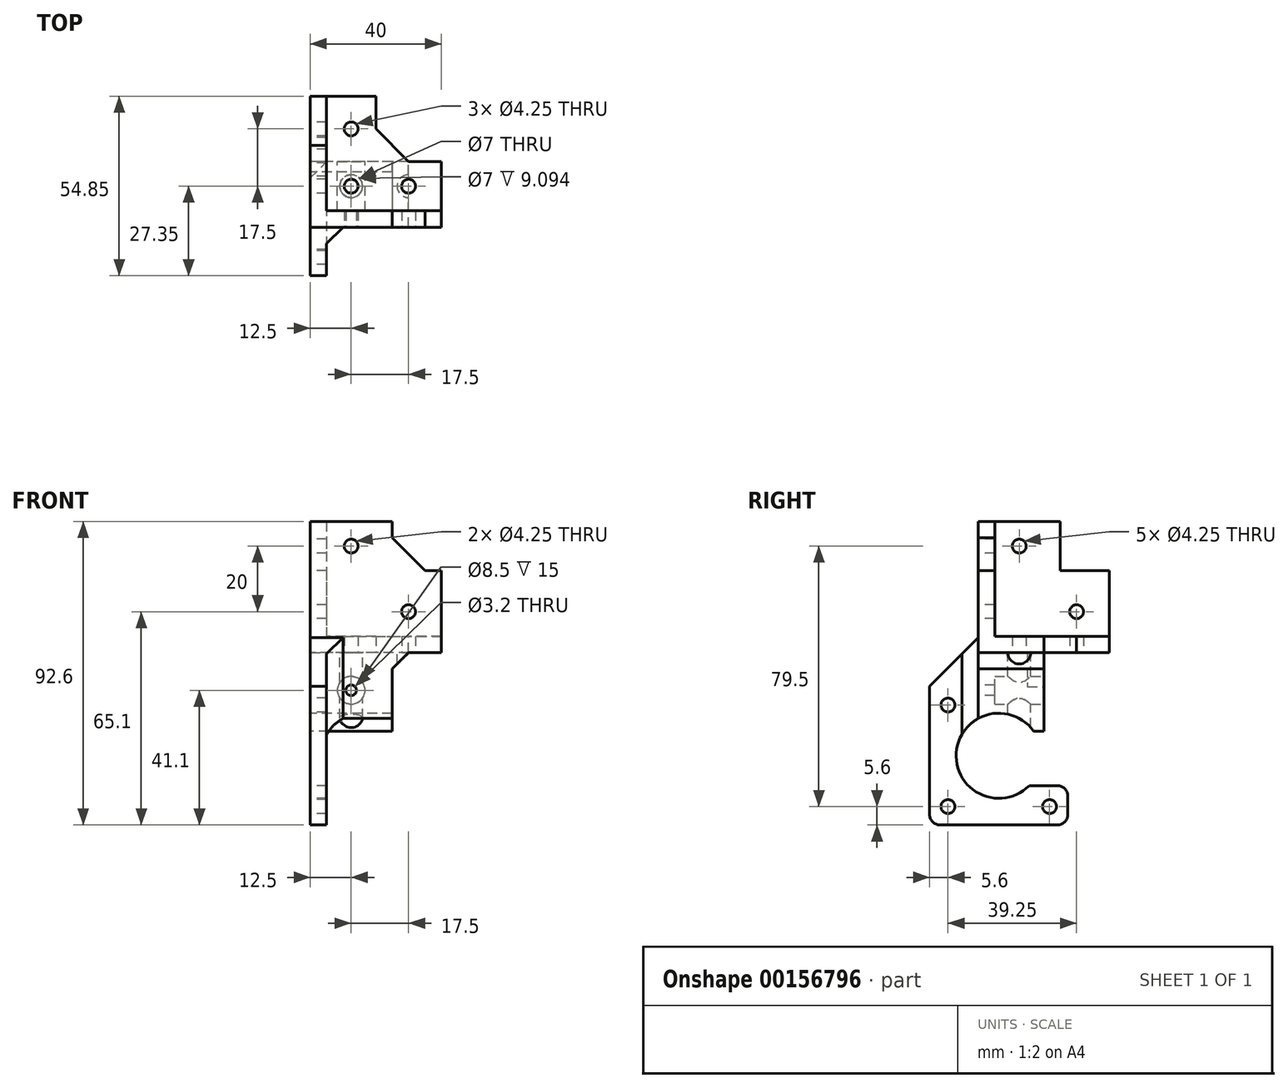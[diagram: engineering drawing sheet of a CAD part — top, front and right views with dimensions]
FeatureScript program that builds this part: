
annotation { "Feature Type Name" : "Feature", "Feature Type Description" : "" }
export const myFeature = defineFeature(function(context is Context, id is Id, definition is map)
    precondition{}
    {
        {
            var Q0;
            Q0=qCreatedBy(makeId("Top.planeOp"),FACE);
            var sketch = newSketch(context, id + "F0", { "sketchPlane" : qUnion([Q0])});
            skLineSegment(sketch, "E0", {"start": v(0, 40) * mm, "end": v(-20, 40) * mm});
            skLineSegment(sketch, "E1", {"start": v(-20, 40) * mm, "end": v(-20, 0) * mm});
            skLineSegment(sketch, "E2", {"start": v(-20, 0) * mm, "end": v(20, 0) * mm});
            skLineSegment(sketch, "E3", {"start": v(20, 0) * mm, "end": v(20, 20) * mm});
            skLineSegment(sketch, "E4", {"start": v(20, 20) * mm, "end": v(0, 20) * mm});
            skLineSegment(sketch, "E5", {"start": v(0, 20) * mm, "end": v(0, 40) * mm});
            skCircle(sketch, "E6", {"center": v(-7.5, 30) * mm, "radius": 2.12 * mm});
            skCircle(sketch, "E7", {"center": v(10, 12.5) * mm, "radius": 2.12 * mm});
            skCircle(sketch, "E8", {"center": v(-7.5, 12.5) * mm, "radius": 2.12 * mm});
            skSolve(sketch);
        }
        {
            var Q0;
            Q0=qSketchRegion(id+"F0",true);
            extrude(context, id + "F1", {"entities" : qUnion([Q0]), "depth" : 5 * mm});
        }
        {
            var Q0;
            Q0=makeQuery(id+"F1.opExtrude","CAP_FACE",FACE,{"disambiguationData":[OSD([sQuery(id+"F0.wireOp",EDGE,"E0"),sQuery(id+"F0.wireOp",EDGE,"E1"),sQuery(id+"F0.wireOp",EDGE,"E2"),sQuery(id+"F0.wireOp",EDGE,"E3"),sQuery(id+"F0.wireOp",EDGE,"E4"),sQuery(id+"F0.wireOp",EDGE,"E5"),sQuery(id+"F0.wireOp",EDGE,"E6"),sQuery(id+"F0.wireOp",EDGE,"E7")])],"isStart":false});
            var sketch = newSketch(context, id + "F2", { "sketchPlane" : qUnion([Q0])});
            skLineSegment(sketch, "E9", {"start": v(-20, 40) * mm, "end": v(-15, 40) * mm});
            skLineSegment(sketch, "E10", {"start": v(-15, 40) * mm, "end": v(-15, 5) * mm});
            skLineSegment(sketch, "E11", {"start": v(-15, 5) * mm, "end": v(20, 5) * mm});
            skLineSegment(sketch, "E12", {"start": v(20, 5) * mm, "end": v(20, 0) * mm});
            skLineSegment(sketch, "E13", {"start": v(20, 0) * mm, "end": v(-20, 0) * mm});
            skLineSegment(sketch, "E14", {"start": v(-20, 0) * mm, "end": v(-20, 40) * mm});
            skSolve(sketch);
        }
        {
            var Q0;
            Q0=qSketchRegion(id+"F2",true);
            extrude(context, id + "F3", {"entities" : qUnion([Q0]), "operationType" : NewBodyOperationType.ADD, "depth" : 20 * mm});
        }
        {
            var Q0;
            Q0=makeQuery(id+"F3.opExtrude","CAP_FACE",FACE,{"disambiguationData":[OSD([sQuery(id+"F2.wireOp",EDGE,"E9"),sQuery(id+"F2.wireOp",EDGE,"E10"),sQuery(id+"F2.wireOp",EDGE,"E11"),sQuery(id+"F2.wireOp",EDGE,"E12"),sQuery(id+"F2.wireOp",EDGE,"E13"),sQuery(id+"F2.wireOp",EDGE,"E14")])],"isStart":false});
            var sketch = newSketch(context, id + "F4", { "sketchPlane" : qUnion([Q0])});
            skLineSegment(sketch, "E15", {"start": v(-15, 25) * mm, "end": v(-20, 25) * mm});
            skLineSegment(sketch, "E16", {"start": v(-20, 25) * mm, "end": v(-20, 0) * mm});
            skLineSegment(sketch, "E17", {"start": v(-20, 0) * mm, "end": v(5, 0) * mm});
            skLineSegment(sketch, "E18", {"start": v(5, 0) * mm, "end": v(5, 5) * mm});
            skLineSegment(sketch, "E19", {"start": v(5, 5) * mm, "end": v(-15, 5) * mm});
            skLineSegment(sketch, "E20", {"start": v(-15, 5) * mm, "end": v(-15, 25) * mm});
            skSolve(sketch);
        }
        {
            var Q0;
            Q0=qSketchRegion(id+"F4",true);
            extrude(context, id + "F5", {"entities" : qUnion([Q0]), "operationType" : NewBodyOperationType.ADD, "depth" : 15 * mm});
        }
        {
            var Q0;
            Q0=makeQuery(id+"F1.opExtrude","SWEPT_EDGE",EDGE,{"disambiguationData":[OSD([sQuery(id+"F0.wireOp",EDGE,"E4"),sQuery(id+"F0.wireOp",EDGE,"E5")])]});
            var Q1;
            Q1=makeQuery(id+"F5.opExtrude","CAP_EDGE",EDGE,{"disambiguationData":[OSD([sQuery(id+"F4.wireOp",EDGE,"E15")])],"isStart":true});
            var Q2;
            Q2=makeQuery(id+"F5.opExtrude","CAP_EDGE",EDGE,{"disambiguationData":[OSD([sQuery(id+"F4.wireOp",EDGE,"E18")])],"isStart":true});
            chamfer(context, id + "F6", {"entities" : qUnion([Q0, Q1, Q2]), "width" : 10 * mm, "tangentPropagation" : true});
        }
        {
            var Q0;
            Q0=makeQuery(id+"F5.boolean.opBoolean","MERGE",FACE,{"derivedFrom":[makeQuery(id+"F3.boolean.opBoolean","MERGE",FACE,{"derivedFrom":[makeQuery(id+"F1.opExtrude","SWEPT_FACE",FACE,{"disambiguationData":[OSD([sQuery(id+"F0.wireOp",EDGE,"E2")])]}),makeQuery(id+"F3.opExtrude","SWEPT_FACE",FACE,{"disambiguationData":[OSD([sQuery(id+"F2.wireOp",EDGE,"E13")])]})]}),makeQuery(id+"F5.opExtrude","SWEPT_FACE",FACE,{"disambiguationData":[OSD([sQuery(id+"F4.wireOp",EDGE,"E17")])]})]});
            var sketch = newSketch(context, id + "F7", { "sketchPlane" : qUnion([Q0])});
            skCircle(sketch, "E21", {"center": v(-7.5, 32.5) * mm, "radius": 2.12 * mm});
            skCircle(sketch, "E22", {"center": v(10, 12.5) * mm, "radius": 2.12 * mm});
            skSolve(sketch);
        }
        {
            var Q0;
            Q0=qSketchRegion(id+"F7",true);
            extrude(context, id + "F8", {"entities" : qUnion([Q0]), "operationType" : NewBodyOperationType.REMOVE, "oppositeDirection" : true, "depth" : 5 * mm});
        }
        {
            var Q0;
            Q0=makeQuery(id+"F5.boolean.opBoolean","MERGE",FACE,{"derivedFrom":[makeQuery(id+"F3.boolean.opBoolean","MERGE",FACE,{"derivedFrom":[makeQuery(id+"F1.opExtrude","SWEPT_FACE",FACE,{"disambiguationData":[OSD([sQuery(id+"F0.wireOp",EDGE,"E1")])]}),makeQuery(id+"F3.opExtrude","SWEPT_FACE",FACE,{"disambiguationData":[OSD([sQuery(id+"F2.wireOp",EDGE,"E14")])]})]}),makeQuery(id+"F5.opExtrude","SWEPT_FACE",FACE,{"disambiguationData":[OSD([sQuery(id+"F4.wireOp",EDGE,"E16")])]})]});
            var sketch = newSketch(context, id + "F9", { "sketchPlane" : qUnion([Q0])});
            skCircle(sketch, "E23", {"center": v(-12.5, 32.5) * mm, "radius": 2.12 * mm});
            skCircle(sketch, "E24", {"center": v(-30, 12.5) * mm, "radius": 2.12 * mm});
            skSolve(sketch);
        }
        {
            var Q0;
            Q0=qSketchRegion(id+"F9",true);
            extrude(context, id + "F10", {"entities" : qUnion([Q0]), "operationType" : NewBodyOperationType.REMOVE, "oppositeDirection" : true, "depth" : 5 * mm});
        }
        {
            var Q0;
            Q0=makeQuery(id+"F1.opExtrude","CAP_FACE",FACE,{"disambiguationData":[OSD([sQuery(id+"F0.wireOp",EDGE,"E0"),sQuery(id+"F0.wireOp",EDGE,"E1"),sQuery(id+"F0.wireOp",EDGE,"E2"),sQuery(id+"F0.wireOp",EDGE,"E3"),sQuery(id+"F0.wireOp",EDGE,"E4"),sQuery(id+"F0.wireOp",EDGE,"E5"),sQuery(id+"F0.wireOp",EDGE,"E6"),sQuery(id+"F0.wireOp",EDGE,"E7"),sQuery(id+"F0.wireOp",EDGE,"E8")])],"isStart":true});
            var sketch = newSketch(context, id + "F11", { "sketchPlane" : qUnion([Q0])});
            skLineSegment(sketch, "E25.bottom", {"start": v(20, -20) * mm, "end": v(-20, -20) * mm});
            skLineSegment(sketch, "E25.top", {"start": v(20, 0) * mm, "end": v(-20, 0) * mm});
            skLineSegment(sketch, "E25.left", {"start": v(20, -20) * mm, "end": v(20, 0) * mm});
            skLineSegment(sketch, "E25.right", {"start": v(-20, -20) * mm, "end": v(-20, 0) * mm});
            skPoint(sketch, "E25.middle", {"position": v(0, -10) * mm});
            skPoint(sketch, "E26.visualSharp", {"position": v(-20, 0) * mm});
            skLineSegment(sketch, "E26.filletArc", {"start": v(-20, 0) * mm, "end": v(-20, 0) * mm});
            skCircle(sketch, "E27", {"center": v(10, -12.5) * mm, "radius": 2.12 * mm});
            skCircle(sketch, "E28", {"center": v(-7.5, -12.5) * mm, "radius": 2.12 * mm});
            skSolve(sketch);
        }
        {
            var Q0;
            Q0=qSketchRegion(id+"F11",true);
            extrude(context, id + "F12", {"entities" : qUnion([Q0]), "operationType" : NewBodyOperationType.ADD, "depth" : 24 * mm});
        }
        {
            var Q0;
            Q0=makeQuery(id+"F12.boolean.opBoolean","MERGE",FACE,{"derivedFrom":[makeQuery(id+"F1.opExtrude","SWEPT_FACE",FACE,{"disambiguationData":[OSD([sQuery(id+"F0.wireOp",EDGE,"E4")])]}),makeQuery(id+"F12.opExtrude","SWEPT_FACE",FACE,{"disambiguationData":[OSD([sQuery(id+"F11.wireOp",EDGE,"E25.bottom")])]})]});
            var sketch = newSketch(context, id + "F13", { "sketchPlane" : qUnion([Q0])});
            skLineSegment(sketch, "E29", {"start": v(20, -11.5) * mm, "end": v(20, -24) * mm});
            skLineSegment(sketch, "E30", {"start": v(20, -24) * mm, "end": v(7.5, -24) * mm});
            skPoint(sketch, "E31.orphan", {"position": v(7.5, -24) * mm});
            skCircle(sketch, "E32", {"center": v(7.5, -11.5) * mm, "radius": 4.25 * mm});
            skLineSegment(sketch, "E33", {"start": v(-5, -11.5) * mm, "end": v(-5, 0) * mm});
            skLineSegment(sketch, "E34", {"start": v(-5, 0) * mm, "end": v(-20, 0) * mm});
            skLineSegment(sketch, "E35", {"start": v(-20, 0) * mm, "end": v(-20, -24) * mm});
            skLineSegment(sketch, "E36", {"start": v(-20, -24) * mm, "end": v(7.5, -24) * mm});
            skLineSegment(sketch, "E37", {"start": v(-5, -11.5) * mm, "end": v(-5, -24) * mm});
            skSolve(sketch);
        }
        {
            var Q0;
            Q0=qSketchRegion(id+"F13",true);
            extrude(context, id + "F14", {"entities" : qUnion([Q0]), "operationType" : NewBodyOperationType.REMOVE, "oppositeDirection" : true, "depth" : 25 * mm});
        }
        {
            var Q0;
            Q0=makeQuery(id+"F14.boolean.opBoolean","MERGE",FACE,{"derivedFrom":[makeQuery(id+"F1.opExtrude","CAP_FACE",FACE,{"disambiguationData":[OSD([sQuery(id+"F0.wireOp",EDGE,"E0"),sQuery(id+"F0.wireOp",EDGE,"E1"),sQuery(id+"F0.wireOp",EDGE,"E2"),sQuery(id+"F0.wireOp",EDGE,"E3"),sQuery(id+"F0.wireOp",EDGE,"E4"),sQuery(id+"F0.wireOp",EDGE,"E5"),sQuery(id+"F0.wireOp",EDGE,"E6"),sQuery(id+"F0.wireOp",EDGE,"E7"),sQuery(id+"F0.wireOp",EDGE,"E8")])],"isStart":true}),makeQuery(id+"F14.opExtrude","SWEPT_FACE",FACE,{"disambiguationData":[OSD([sQuery(id+"F13.wireOp",EDGE,"E34")])]})]});
            var sketch = newSketch(context, id + "F15", { "sketchPlane" : qUnion([Q0])});
            skCircle(sketch, "E38", {"center": v(-7.5, -12.5) * mm, "radius": 3.5 * mm});
            skSolve(sketch);
        }
        {
            var Q0;
            Q0=qSketchRegion(id+"F15",true);
            extrude(context, id + "F16", {"entities" : qUnion([Q0]), "operationType" : NewBodyOperationType.REMOVE, "depth" : 25 * mm});
        }
        {
            var Q0;
            Q0=makeQuery(id+"F12.boolean.opBoolean","MERGE",FACE,{"derivedFrom":[makeQuery(id+"F5.boolean.opBoolean","MERGE",FACE,{"derivedFrom":[makeQuery(id+"F3.boolean.opBoolean","MERGE",FACE,{"derivedFrom":[makeQuery(id+"F1.opExtrude","SWEPT_FACE",FACE,{"disambiguationData":[OSD([sQuery(id+"F0.wireOp",EDGE,"E2")])]}),makeQuery(id+"F3.opExtrude","SWEPT_FACE",FACE,{"disambiguationData":[OSD([sQuery(id+"F2.wireOp",EDGE,"E13")])]})]}),makeQuery(id+"F5.opExtrude","SWEPT_FACE",FACE,{"disambiguationData":[OSD([sQuery(id+"F4.wireOp",EDGE,"E17")])]})]}),makeQuery(id+"F12.opExtrude","SWEPT_FACE",FACE,{"disambiguationData":[OSD([sQuery(id+"F11.wireOp",EDGE,"E25.top")])]})]});
            var sketch = newSketch(context, id + "F17", { "sketchPlane" : qUnion([Q0])});
            skCircle(sketch, "E39", {"center": v(-7.5, -11.5) * mm, "radius": 4.25 * mm});
            skCircle(sketch, "E40", {"center": v(-7.5, -11.5) * mm, "radius": 1.6 * mm});
            skSolve(sketch);
        }
        {
            var Q0;
            Q0=qSketchRegion(id+"F17",true);
            extrude(context, id + "F18", {"entities" : qUnion([Q0]), "operationType" : NewBodyOperationType.ADD, "oppositeDirection" : true, "depth" : 5 * mm});
        }
        {
            var Q0;
            Q0=makeQuery(id+"FNQfyr8qSEigWVF_1.boolean.opBoolean","MERGE",EDGE,{"derivedFrom":[makeQuery(id+"F14.boolean.opBoolean","COPY",EDGE,{"derivedFrom":makeQuery(id+"F14.opExtrude","SWEPT_EDGE",EDGE,{"disambiguationData":[OSD([sQuery(id+"F11.wireOp",EDGE,"E25.bottom"),sQuery(id+"F13.wireOp",EDGE,"E33"),sQuery(id+"F13.wireOp",EDGE,"E34")])]})}),makeQuery(id+"FNQfyr8qSEigWVF_1.opExtrude","SWEPT_EDGE",EDGE,{"disambiguationData":[OSD([sQuery(id+"F1wlyD548anW5wl_1.wireOp",EDGE,"YZkgPk9V-HXlL-QKvk-AvvO-C27N44Z9oYY3.bottom"),sQuery(id+"F1wlyD548anW5wl_1.wireOp",EDGE,"YZkgPk9V-HXlL-QKvk-AvvO-C27N44Z9oYY3.left")])]})]});
            chamfer(context, id + "F19", {"entities" : qUnion([Q0]), "width" : 5 * mm, "tangentPropagation" : true});
        }
        {
            var Q0;
            Q0=makeQuery(id+"F18.boolean.opBoolean","MERGE",FACE,{"derivedFrom":[makeQuery(id+"F12.boolean.opBoolean","MERGE",FACE,{"derivedFrom":[makeQuery(id+"F5.boolean.opBoolean","MERGE",FACE,{"derivedFrom":[makeQuery(id+"F3.boolean.opBoolean","MERGE",FACE,{"derivedFrom":[makeQuery(id+"F1.opExtrude","SWEPT_FACE",FACE,{"disambiguationData":[OSD([sQuery(id+"F0.wireOp",EDGE,"E2")])]}),makeQuery(id+"F3.opExtrude","SWEPT_FACE",FACE,{"disambiguationData":[OSD([sQuery(id+"F2.wireOp",EDGE,"E13")])]})]}),makeQuery(id+"F5.opExtrude","SWEPT_FACE",FACE,{"disambiguationData":[OSD([sQuery(id+"F4.wireOp",EDGE,"E17")])]})]}),makeQuery(id+"F12.opExtrude","SWEPT_FACE",FACE,{"disambiguationData":[OSD([sQuery(id+"F11.wireOp",EDGE,"E25.top")])]})]}),makeQuery(id+"F18.opExtrude","CAP_FACE",FACE,{"disambiguationData":[OSD([sQuery(id+"F17.wireOp",EDGE,"E39"),sQuery(id+"F17.wireOp",EDGE,"E40")])],"isStart":true})]});
            var sketch = newSketch(context, id + "F20", { "sketchPlane" : qUnion([Q0])});
            skLineSegment(sketch, "E41", {"start": v(-20, -24) * mm, "end": v(-20, -44) * mm});
            skLineSegment(sketch, "E42", {"start": v(-20, -44) * mm, "end": v(5, -44) * mm});
            skLineSegment(sketch, "E43", {"start": v(5, -44) * mm, "end": v(5, -24) * mm});
            skLineSegment(sketch, "E44", {"start": v(5, -24) * mm, "end": v(-2.75, -24) * mm});
            skLineSegment(sketch, "E45", {"start": v(-2.75, -24) * mm, "end": v(-2.75, -39) * mm});
            skLineSegment(sketch, "E46", {"start": v(-2.75, -39) * mm, "end": v(-12.25, -39) * mm});
            skLineSegment(sketch, "E47", {"start": v(-12.25, -39) * mm, "end": v(-12.25, -24) * mm});
            skLineSegment(sketch, "E48", {"start": v(-12.25, -24) * mm, "end": v(-20, -24) * mm});
            skSolve(sketch);
        }
        {
            var Q0;
            Q0=qSketchRegion(id+"F20",true);
            extrude(context, id + "F21", {"entities" : qUnion([Q0]), "operationType" : NewBodyOperationType.ADD, "oppositeDirection" : true, "depth" : 12.5 * mm});
        }
        {
            var Q0;
            Q0=makeQuery(id+"F21.opExtrude","SWEPT_EDGE",EDGE,{"disambiguationData":[OSD([sQuery(id+"F20.wireOp",EDGE,"E41"),sQuery(id+"F20.wireOp",EDGE,"E42")])]});
            var Q1;
            Q1=makeQuery(id+"F21.opExtrude","SWEPT_EDGE",EDGE,{"disambiguationData":[OSD([sQuery(id+"F20.wireOp",EDGE,"E42"),sQuery(id+"F20.wireOp",EDGE,"E43")])]});
            var Q2;
            Q2=makeQuery(id+"F14.boolean.opBoolean","COPY",EDGE,{"derivedFrom":makeQuery(id+"F14.opExtrude","CAP_EDGE",EDGE,{"disambiguationData":[OSD([sQuery(id+"F13.wireOp",EDGE,"E33"),sQuery(id+"F13.wireOp",EDGE,"E37")])],"isStart":true})});
            var Q3;
            Q3=makeQuery(id+"F12.opExtrude","SWEPT_EDGE",EDGE,{"disambiguationData":[OSD([sQuery(id+"F0.wireOp",EDGE,"E1"),sQuery(id+"F11.wireOp",EDGE,"E25.bottom"),sQuery(id+"F11.wireOp",EDGE,"E25.right")])]});
            chamfer(context, id + "F22", {"entities" : qUnion([Q0, Q1, Q2, Q3]), "width" : 5 * mm, "tangentPropagation" : true});
        }
        {
            var Q0;
            Q0=makeQuery(id+"F19.opChamfer","SPLIT",FACE,{"disambiguationData":[OD(1.0)],"derivedFrom":makeQuery(id+"F14.boolean.opBoolean","MERGE",FACE,{"derivedFrom":[makeQuery(id+"F1.opExtrude","CAP_FACE",FACE,{"disambiguationData":[OSD([sQuery(id+"F0.wireOp",EDGE,"E0"),sQuery(id+"F0.wireOp",EDGE,"E1"),sQuery(id+"F0.wireOp",EDGE,"E2"),sQuery(id+"F0.wireOp",EDGE,"E3"),sQuery(id+"F0.wireOp",EDGE,"E4"),sQuery(id+"F0.wireOp",EDGE,"E5"),sQuery(id+"F0.wireOp",EDGE,"E6"),sQuery(id+"F0.wireOp",EDGE,"E7"),sQuery(id+"F0.wireOp",EDGE,"E8")])],"isStart":true}),makeQuery(id+"F14.opExtrude","SWEPT_FACE",FACE,{"disambiguationData":[OSD([sQuery(id+"F13.wireOp",EDGE,"E34")])]})]})});
            var sketch = newSketch(context, id + "F23", { "sketchPlane" : qUnion([Q0])});
            skCircle(sketch, "E49", {"center": v(10, -12.5) * mm, "radius": 3.5 * mm});
            skSolve(sketch);
        }
        {
            var Q0;
            Q0=qSketchRegion(id+"F23",true);
            extrude(context, id + "F24", {"entities" : qUnion([Q0]), "operationType" : NewBodyOperationType.REMOVE, "endBound" : BoundingType.THROUGH_ALL, "depth" : 25 * mm});
        }
        {
            var Q0;
            Q0=makeQuery(id+"F21.boolean.opBoolean","MERGE",FACE,{"derivedFrom":[makeQuery(id+"F12.boolean.opBoolean","MERGE",FACE,{"derivedFrom":[makeQuery(id+"F5.boolean.opBoolean","MERGE",FACE,{"derivedFrom":[makeQuery(id+"F3.boolean.opBoolean","MERGE",FACE,{"derivedFrom":[makeQuery(id+"F1.opExtrude","SWEPT_FACE",FACE,{"disambiguationData":[OSD([sQuery(id+"F0.wireOp",EDGE,"E1")])]}),makeQuery(id+"F3.opExtrude","SWEPT_FACE",FACE,{"disambiguationData":[OSD([sQuery(id+"F2.wireOp",EDGE,"E14")])]})]}),makeQuery(id+"F5.opExtrude","SWEPT_FACE",FACE,{"disambiguationData":[OSD([sQuery(id+"F4.wireOp",EDGE,"E16")])]})]}),makeQuery(id+"F12.opExtrude","SWEPT_FACE",FACE,{"disambiguationData":[OSD([sQuery(id+"F11.wireOp",EDGE,"E25.right")])]})]}),makeQuery(id+"F21.opExtrude","SWEPT_FACE",FACE,{"disambiguationData":[OSD([sQuery(id+"F20.wireOp",EDGE,"E41")])]})]});
            var sketch = newSketch(context, id + "F25", { "sketchPlane" : qUnion([Q0])});
            skCircle(sketch, "E50", {"center": v(-6.25, -31.5) * mm, "radius": 2.12 * mm});
            skSolve(sketch);
        }
        {
            var Q0;
            Q0=qSketchRegion(id+"F25",true);
            extrude(context, id + "F26", {"entities" : qUnion([Q0]), "operationType" : NewBodyOperationType.REMOVE, "endBound" : BoundingType.THROUGH_ALL, "oppositeDirection" : true, "depth" : 25 * mm});
        }
        {
            var Q0;
            Q0=makeQuery(id+"F21.boolean.opBoolean","MERGE",FACE,{"derivedFrom":[makeQuery(id+"F12.boolean.opBoolean","MERGE",FACE,{"derivedFrom":[makeQuery(id+"F5.boolean.opBoolean","MERGE",FACE,{"derivedFrom":[makeQuery(id+"F3.boolean.opBoolean","MERGE",FACE,{"derivedFrom":[makeQuery(id+"F1.opExtrude","SWEPT_FACE",FACE,{"disambiguationData":[OSD([sQuery(id+"F0.wireOp",EDGE,"E1")])]}),makeQuery(id+"F3.opExtrude","SWEPT_FACE",FACE,{"disambiguationData":[OSD([sQuery(id+"F2.wireOp",EDGE,"E14")])]})]}),makeQuery(id+"F5.opExtrude","SWEPT_FACE",FACE,{"disambiguationData":[OSD([sQuery(id+"F4.wireOp",EDGE,"E16")])]})]}),makeQuery(id+"F12.opExtrude","SWEPT_FACE",FACE,{"disambiguationData":[OSD([sQuery(id+"F11.wireOp",EDGE,"E25.right")])]})]}),makeQuery(id+"F21.opExtrude","SWEPT_FACE",FACE,{"disambiguationData":[OSD([sQuery(id+"F20.wireOp",EDGE,"E41")])]})]});
            var sketch = newSketch(context, id + "F27", { "sketchPlane" : qUnion([Q0])});
            skCircle(sketch, "E51.cCircle", {"center": v(-6.25, -31.5) * mm, "radius": 2.93 * mm, "construction": true});
            skLineSegment(sketch, "E51.0", {"start": v(-3.33, -29.81) * mm, "end": v(-3.33, -33.19) * mm});
            skLineSegment(sketch, "E51.1", {"start": v(-3.33, -33.19) * mm, "end": v(-6.25, -34.88) * mm});
            skLineSegment(sketch, "E51.2", {"start": v(-6.25, -34.88) * mm, "end": v(-9.17, -33.19) * mm});
            skLineSegment(sketch, "E51.3", {"start": v(-9.18, -33.19) * mm, "end": v(-9.18, -29.81) * mm});
            skLineSegment(sketch, "E51.4", {"start": v(-9.17, -29.81) * mm, "end": v(-6.25, -28.12) * mm});
            skLineSegment(sketch, "E51.5", {"start": v(-6.25, -28.12) * mm, "end": v(-3.33, -29.81) * mm});
            skPoint(sketch, "E51.0.midPoint", {"position": v(-3.33, -31.5) * mm});
            skSolve(sketch);
        }
        {
            var Q0;
            Q0=qSketchRegion(id+"F27",true);
            extrude(context, id + "F28", {"entities" : qUnion([Q0]), "operationType" : NewBodyOperationType.REMOVE, "oppositeDirection" : true, "depth" : 4 * mm});
        }
        {
            var Q0;
            Q0=makeQuery(id+"F21.boolean.opBoolean","MERGE",FACE,{"derivedFrom":[makeQuery(id+"F14.boolean.opBoolean","COPY",FACE,{"derivedFrom":makeQuery(id+"F14.opExtrude","SWEPT_FACE",FACE,{"disambiguationData":[OSD([sQuery(id+"F13.wireOp",EDGE,"E33"),sQuery(id+"F13.wireOp",EDGE,"E37")])]})}),makeQuery(id+"F21.opExtrude","SWEPT_FACE",FACE,{"disambiguationData":[OSD([sQuery(id+"F20.wireOp",EDGE,"E43")])]})]});
            var sketch = newSketch(context, id + "F29", { "sketchPlane" : qUnion([Q0])});
            skCircle(sketch, "E52", {"center": v(6.25, -31.5) * mm, "radius": 3.5 * mm});
            skSolve(sketch);
        }
        {
            var Q0;
            Q0=qSketchRegion(id+"F29",true);
            extrude(context, id + "F30", {"entities" : qUnion([Q0]), "operationType" : NewBodyOperationType.REMOVE, "oppositeDirection" : true, "depth" : 4 * mm});
        }
        {
            var Q0;
            Q0=makeQuery(id+"F21.boolean.opBoolean","MERGE",FACE,{"derivedFrom":[makeQuery(id+"F12.boolean.opBoolean","MERGE",FACE,{"derivedFrom":[makeQuery(id+"F5.boolean.opBoolean","MERGE",FACE,{"derivedFrom":[makeQuery(id+"F3.boolean.opBoolean","MERGE",FACE,{"derivedFrom":[makeQuery(id+"F1.opExtrude","SWEPT_FACE",FACE,{"disambiguationData":[OSD([sQuery(id+"F0.wireOp",EDGE,"E1")])]}),makeQuery(id+"F3.opExtrude","SWEPT_FACE",FACE,{"disambiguationData":[OSD([sQuery(id+"F2.wireOp",EDGE,"E14")])]})]}),makeQuery(id+"F5.opExtrude","SWEPT_FACE",FACE,{"disambiguationData":[OSD([sQuery(id+"F4.wireOp",EDGE,"E16")])]})]}),makeQuery(id+"F12.opExtrude","SWEPT_FACE",FACE,{"disambiguationData":[OSD([sQuery(id+"F11.wireOp",EDGE,"E25.right")])]})]}),makeQuery(id+"F21.opExtrude","SWEPT_FACE",FACE,{"disambiguationData":[OSD([sQuery(id+"F20.wireOp",EDGE,"E41")])]})]});
            var sketch = newSketch(context, id + "F31", { "sketchPlane" : qUnion([Q0])});
            skLineSegment(sketch, "E53.bottom", {"start": v(0, -44) * mm, "end": v(-12.5, -44) * mm});
            skLineSegment(sketch, "E53.top", {"start": v(0, -24) * mm, "end": v(-12.5, -24) * mm});
            skLineSegment(sketch, "E53.left", {"start": v(0, -44) * mm, "end": v(0, -24) * mm});
            skLineSegment(sketch, "E53.right", {"start": v(-12.5, -44) * mm, "end": v(-12.5, -24) * mm});
            skPoint(sketch, "E53.middle", {"position": v(-6.25, -34) * mm});
            skSolve(sketch);
        }
        {
            var Q0;
            Q0=qSketchRegion(id+"F31",true);
            extrude(context, id + "F32", {"entities" : qUnion([Q0]), "operationType" : NewBodyOperationType.REMOVE, "endBound" : BoundingType.THROUGH_ALL, "oppositeDirection" : true, "depth" : 25 * mm});
        }
        {
            var Q0;
            Q0=makeQuery(id+"F21.boolean.opBoolean","MERGE",FACE,{"derivedFrom":[makeQuery(id+"F12.boolean.opBoolean","MERGE",FACE,{"derivedFrom":[makeQuery(id+"F5.boolean.opBoolean","MERGE",FACE,{"derivedFrom":[makeQuery(id+"F3.boolean.opBoolean","MERGE",FACE,{"derivedFrom":[makeQuery(id+"F1.opExtrude","SWEPT_FACE",FACE,{"disambiguationData":[OSD([sQuery(id+"F0.wireOp",EDGE,"E1")])]}),makeQuery(id+"F3.opExtrude","SWEPT_FACE",FACE,{"disambiguationData":[OSD([sQuery(id+"F2.wireOp",EDGE,"E14")])]})]}),makeQuery(id+"F5.opExtrude","SWEPT_FACE",FACE,{"disambiguationData":[OSD([sQuery(id+"F4.wireOp",EDGE,"E16")])]})]}),makeQuery(id+"F12.opExtrude","SWEPT_FACE",FACE,{"disambiguationData":[OSD([sQuery(id+"F11.wireOp",EDGE,"E25.right")])]})]}),makeQuery(id+"F21.opExtrude","SWEPT_FACE",FACE,{"disambiguationData":[OSD([sQuery(id+"F20.wireOp",EDGE,"E41")])]})]});
            var sketch = newSketch(context, id + "F33", { "sketchPlane" : qUnion([Q0])});
            skArc(sketch, "E54", {"start": v(-15.53, -40.6) * mm, "mid": v(6.7, -30.46) * mm, "end": v(-16.87, -24) * mm});
            skLineSegment(sketch, "E55.bottom", {"start": v(14.85, -52.6) * mm, "end": v(-27.35, -52.6) * mm});
            skLineSegment(sketch, "E55.top", {"start": v(14.85, -10.4) * mm, "end": v(-20, -10.4) * mm});
            skLineSegment(sketch, "E55.left", {"start": v(14.85, -52.6) * mm, "end": v(14.85, -10.4) * mm});
            skLineSegment(sketch, "E55.right", {"start": v(-27.35, -52.6) * mm, "end": v(-27.35, -40.6) * mm});
            skLineSegment(sketch, "E56.bottom", {"start": v(9.25, -47) * mm, "end": v(-21.75, -47) * mm, "construction": true});
            skLineSegment(sketch, "E56.top", {"start": v(9.25, -16) * mm, "end": v(-21.75, -16) * mm, "construction": true});
            skLineSegment(sketch, "E56.left", {"start": v(9.25, -47) * mm, "end": v(9.25, -16) * mm, "construction": true});
            skLineSegment(sketch, "E56.right", {"start": v(-21.75, -47) * mm, "end": v(-21.75, -16) * mm, "construction": true});
            skCircle(sketch, "E57", {"center": v(9.25, -16) * mm, "radius": 2.12 * mm});
            skCircle(sketch, "E58", {"center": v(9.25, -47) * mm, "radius": 2.12 * mm});
            skCircle(sketch, "E59", {"center": v(-21.75, -47) * mm, "radius": 2.12 * mm});
            skLineSegment(sketch, "E60", {"start": v(-20, -10.4) * mm, "end": v(-20, -24) * mm});
            skLineSegment(sketch, "E61", {"start": v(-20, -24) * mm, "end": v(-16.87, -24) * mm});
            skLineSegment(sketch, "E62", {"start": v(-15.53, -40.6) * mm, "end": v(-27.35, -40.6) * mm});
            skPoint(sketch, "E63.orphan", {"position": v(-27.35, -10.4) * mm});
            skSolve(sketch);
        }
        {
            var Q0;
            Q0=qSketchRegion(id+"F33",true);
            extrude(context, id + "F34", {"entities" : qUnion([Q0]), "operationType" : NewBodyOperationType.ADD, "oppositeDirection" : true, "depth" : 5 * mm});
        }
        {
            var Q0;
            Q0=makeQuery(id+"F34.boolean.opBoolean","MERGE",FACE,{"derivedFrom":[makeQuery(id+"F21.boolean.opBoolean","MERGE",FACE,{"derivedFrom":[makeQuery(id+"F12.boolean.opBoolean","MERGE",FACE,{"derivedFrom":[makeQuery(id+"F5.boolean.opBoolean","MERGE",FACE,{"derivedFrom":[makeQuery(id+"F3.boolean.opBoolean","MERGE",FACE,{"derivedFrom":[makeQuery(id+"F1.opExtrude","SWEPT_FACE",FACE,{"disambiguationData":[OSD([sQuery(id+"F0.wireOp",EDGE,"E1")])]}),makeQuery(id+"F3.opExtrude","SWEPT_FACE",FACE,{"disambiguationData":[OSD([sQuery(id+"F2.wireOp",EDGE,"E14")])]})]}),makeQuery(id+"F5.opExtrude","SWEPT_FACE",FACE,{"disambiguationData":[OSD([sQuery(id+"F4.wireOp",EDGE,"E16")])]})]}),makeQuery(id+"F12.opExtrude","SWEPT_FACE",FACE,{"disambiguationData":[OSD([sQuery(id+"F11.wireOp",EDGE,"E25.right")])]})]}),makeQuery(id+"F21.opExtrude","SWEPT_FACE",FACE,{"disambiguationData":[OSD([sQuery(id+"F20.wireOp",EDGE,"E41")])]})]}),makeQuery(id+"F34.opExtrude","CAP_FACE",FACE,{"disambiguationData":[OSD([sQuery(id+"F33.wireOp",EDGE,"E54"),sQuery(id+"F33.wireOp",EDGE,"E55.bottom"),sQuery(id+"F33.wireOp",EDGE,"E55.top"),sQuery(id+"F33.wireOp",EDGE,"E55.left"),sQuery(id+"F33.wireOp",EDGE,"E55.right"),sQuery(id+"F33.wireOp",EDGE,"E57"),sQuery(id+"F33.wireOp",EDGE,"E58"),sQuery(id+"F33.wireOp",EDGE,"E59"),sQuery(id+"F33.wireOp",EDGE,"E60"),sQuery(id+"F33.wireOp",EDGE,"E61"),sQuery(id+"F33.wireOp",EDGE,"E62")])],"isStart":true})]});
            var sketch = newSketch(context, id + "F35", { "sketchPlane" : qUnion([Q0])});
            skCircle(sketch, "E64", {"center": v(-6.25, -31.5) * mm, "radius": 13 * mm});
            skSolve(sketch);
        }
        {
            var Q0;
            Q0=qSketchRegion(id+"F35",true);
            extrude(context, id + "F36", {"entities" : qUnion([Q0]), "operationType" : NewBodyOperationType.REMOVE, "endBound" : BoundingType.THROUGH_ALL, "oppositeDirection" : true, "depth" : 25 * mm});
        }
        {
            var Q0;
            Q0=makeQuery(id+"F34.opExtrude","SWEPT_EDGE",EDGE,{"disambiguationData":[OSD([sQuery(id+"F33.wireOp",EDGE,"E55.right"),sQuery(id+"F33.wireOp",EDGE,"E62")])]});
            var Q1;
            Q1=makeQuery(id+"F34.opExtrude","SWEPT_EDGE",EDGE,{"disambiguationData":[OSD([sQuery(id+"F33.wireOp",EDGE,"E55.bottom"),sQuery(id+"F33.wireOp",EDGE,"E55.right")])]});
            var Q2;
            Q2=makeQuery(id+"F34.opExtrude","SWEPT_EDGE",EDGE,{"disambiguationData":[OSD([sQuery(id+"F33.wireOp",EDGE,"E55.bottom"),sQuery(id+"F33.wireOp",EDGE,"E55.left")])]});
            fillet(context, id + "F37", {"entities" : qUnion([Q0, Q1, Q2]), "radius" : 3.2 * mm, "tangentPropagation" : true, "allowEdgeOverflow" : false});
        }
        {
            var Q0;
            Q0=makeQuery(id+"F34.boolean.opBoolean","INTERSECT",EDGE,{"derivedFrom":[makeQuery(id+"F21.boolean.opBoolean","MERGE",FACE,{"derivedFrom":[makeQuery(id+"F18.boolean.opBoolean","MERGE",FACE,{"derivedFrom":[makeQuery(id+"F12.boolean.opBoolean","MERGE",FACE,{"derivedFrom":[makeQuery(id+"F5.boolean.opBoolean","MERGE",FACE,{"derivedFrom":[makeQuery(id+"F3.boolean.opBoolean","MERGE",FACE,{"derivedFrom":[makeQuery(id+"F1.opExtrude","SWEPT_FACE",FACE,{"disambiguationData":[OSD([sQuery(id+"F0.wireOp",EDGE,"E2")])]}),makeQuery(id+"F3.opExtrude","SWEPT_FACE",FACE,{"disambiguationData":[OSD([sQuery(id+"F2.wireOp",EDGE,"E13")])]})]}),makeQuery(id+"F5.opExtrude","SWEPT_FACE",FACE,{"disambiguationData":[OSD([sQuery(id+"F4.wireOp",EDGE,"E17")])]})]}),makeQuery(id+"F12.opExtrude","SWEPT_FACE",FACE,{"disambiguationData":[OSD([sQuery(id+"F11.wireOp",EDGE,"E25.top")])]})]}),makeQuery(id+"F18.opExtrude","CAP_FACE",FACE,{"disambiguationData":[OSD([sQuery(id+"F17.wireOp",EDGE,"E39"),sQuery(id+"F17.wireOp",EDGE,"E40")])],"isStart":true})]}),makeQuery(id+"F21.opExtrude","CAP_FACE",FACE,{"disambiguationData":[OSD([sQuery(id+"F20.wireOp",EDGE,"E41"),sQuery(id+"F20.wireOp",EDGE,"E42"),sQuery(id+"F20.wireOp",EDGE,"E43"),sQuery(id+"F20.wireOp",EDGE,"E44"),sQuery(id+"F20.wireOp",EDGE,"E45"),sQuery(id+"F20.wireOp",EDGE,"E46"),sQuery(id+"F20.wireOp",EDGE,"E47"),sQuery(id+"F20.wireOp",EDGE,"E48")])],"isStart":true})]}),makeQuery(id+"F34.opExtrude","SWEPT_FACE",FACE,{"disambiguationData":[OSD([sQuery(id+"F33.wireOp",EDGE,"E55.top")])]})]});
            chamfer(context, id + "F38", {"entities" : qUnion([Q0]), "width" : 15 * mm, "tangentPropagation" : true});
        }
        {
            var Q0;
            Q0=makeQuery(id+"F34.boolean.opBoolean","INTERSECT",EDGE,{"derivedFrom":[makeQuery(id+"F21.boolean.opBoolean","MERGE",FACE,{"derivedFrom":[makeQuery(id+"F18.boolean.opBoolean","MERGE",FACE,{"derivedFrom":[makeQuery(id+"F12.boolean.opBoolean","MERGE",FACE,{"derivedFrom":[makeQuery(id+"F5.boolean.opBoolean","MERGE",FACE,{"derivedFrom":[makeQuery(id+"F3.boolean.opBoolean","MERGE",FACE,{"derivedFrom":[makeQuery(id+"F1.opExtrude","SWEPT_FACE",FACE,{"disambiguationData":[OSD([sQuery(id+"F0.wireOp",EDGE,"E2")])]}),makeQuery(id+"F3.opExtrude","SWEPT_FACE",FACE,{"disambiguationData":[OSD([sQuery(id+"F2.wireOp",EDGE,"E13")])]})]}),makeQuery(id+"F5.opExtrude","SWEPT_FACE",FACE,{"disambiguationData":[OSD([sQuery(id+"F4.wireOp",EDGE,"E17")])]})]}),makeQuery(id+"F12.opExtrude","SWEPT_FACE",FACE,{"disambiguationData":[OSD([sQuery(id+"F11.wireOp",EDGE,"E25.top")])]})]}),makeQuery(id+"F18.opExtrude","CAP_FACE",FACE,{"disambiguationData":[OSD([sQuery(id+"F17.wireOp",EDGE,"E39"),sQuery(id+"F17.wireOp",EDGE,"E40")])],"isStart":true})]}),makeQuery(id+"F21.opExtrude","CAP_FACE",FACE,{"disambiguationData":[OSD([sQuery(id+"F20.wireOp",EDGE,"E41"),sQuery(id+"F20.wireOp",EDGE,"E42"),sQuery(id+"F20.wireOp",EDGE,"E43"),sQuery(id+"F20.wireOp",EDGE,"E44"),sQuery(id+"F20.wireOp",EDGE,"E45"),sQuery(id+"F20.wireOp",EDGE,"E46"),sQuery(id+"F20.wireOp",EDGE,"E47"),sQuery(id+"F20.wireOp",EDGE,"E48")])],"isStart":true})]}),makeQuery(id+"F34.opExtrude","CAP_FACE",FACE,{"disambiguationData":[OSD([sQuery(id+"F33.wireOp",EDGE,"E54"),sQuery(id+"F33.wireOp",EDGE,"E55.bottom"),sQuery(id+"F33.wireOp",EDGE,"E55.top"),sQuery(id+"F33.wireOp",EDGE,"E55.left"),sQuery(id+"F33.wireOp",EDGE,"E55.right"),sQuery(id+"F33.wireOp",EDGE,"E57"),sQuery(id+"F33.wireOp",EDGE,"E58"),sQuery(id+"F33.wireOp",EDGE,"E59"),sQuery(id+"F33.wireOp",EDGE,"E60"),sQuery(id+"F33.wireOp",EDGE,"E61"),sQuery(id+"F33.wireOp",EDGE,"E62")])],"isStart":false})]});
            chamfer(context, id + "F39", {"entities" : qUnion([Q0]), "width" : 5 * mm, "tangentPropagation" : true});
        }
    });
